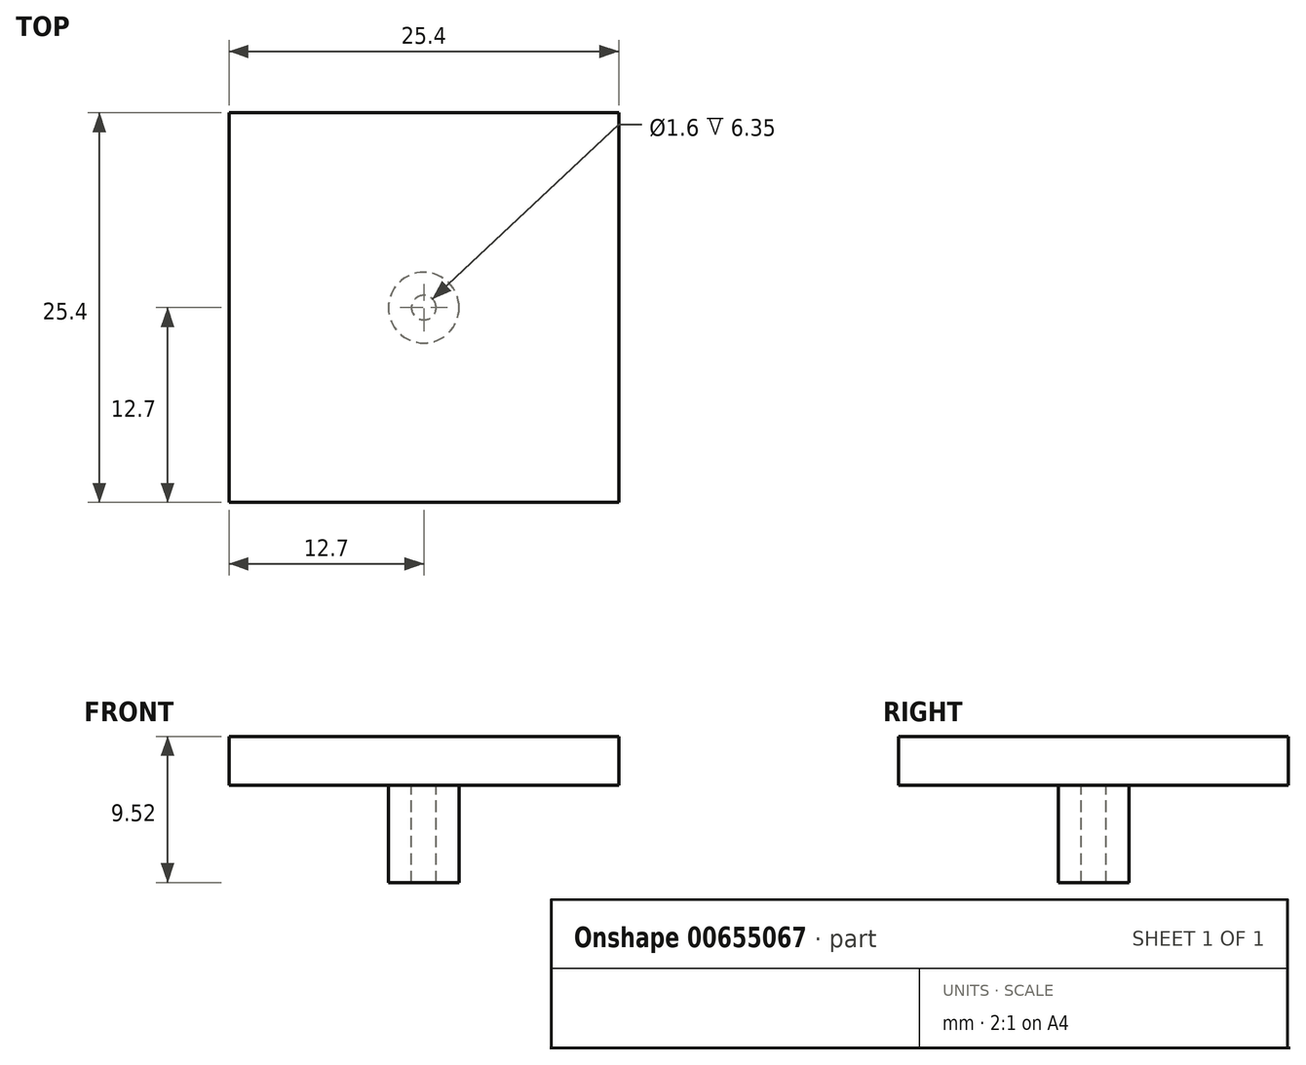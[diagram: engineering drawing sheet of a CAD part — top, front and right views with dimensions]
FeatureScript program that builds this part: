
annotation { "Feature Type Name" : "Feature", "Feature Type Description" : "" }
export const myFeature = defineFeature(function(context is Context, id is Id, definition is map)
    precondition{}
    {
        {
            var Q0;
            Q0=qCreatedBy(makeId("Top.planeOp"),FACE);
            var sketch = newSketch(context, id + "F0", { "sketchPlane" : qUnion([Q0])});
            skLineSegment(sketch, "E0.bottom", {"start": v(0, 25.4) * mm, "end": v(25.4, 25.4) * mm});
            skLineSegment(sketch, "E0.top", {"start": v(0, 0) * mm, "end": v(25.4, 0) * mm});
            skLineSegment(sketch, "E0.left", {"start": v(0, 25.4) * mm, "end": v(0, 0) * mm});
            skLineSegment(sketch, "E0.right", {"start": v(25.4, 25.4) * mm, "end": v(25.4, 0) * mm});
            skCircle(sketch, "E1", {"center": v(12.7, 12.7) * mm, "radius": 0.8 * mm});
            skCircle(sketch, "E2", {"center": v(12.7, 12.7) * mm, "radius": 2.3 * mm});
            skSolve(sketch);
        }
        {
            var Q0;
            Q0=makeQuery(id+"F0.imprint","IMPRINT",FACE,{"disambiguationData":[TD([[makeQuery(id+"F0.imprint","IMPRINT",EDGE,{"derivedFrom":sQuery(id+"F0.wireOp",EDGE,"E0.bottom")}),-1.0]])]});
            var Q1;
            Q1=makeQuery(id+"F0.imprint","IMPRINT",FACE,{"disambiguationData":[TD([[makeQuery(id+"F0.imprint","IMPRINT",EDGE,{"derivedFrom":sQuery(id+"F0.wireOp",EDGE,"E1")}),-1.0]])]});
            var Q2;
            Q2=makeQuery(id+"F0.imprint","IMPRINT",FACE,{"disambiguationData":[TD([[makeQuery(id+"F0.imprint","IMPRINT",EDGE,{"derivedFrom":sQuery(id+"F0.wireOp",EDGE,"E1")}),1.0]])]});
            extrude(context, id + "F1", {"entities" : qUnion([Q0, Q1, Q2]), "depth" : 3.17 * mm, "offsetDistance" : 25.4 * mm});
        }
        {
            var Q0;
            Q0=makeQuery(id+"F0.imprint","IMPRINT",FACE,{"disambiguationData":[TD([[makeQuery(id+"F0.imprint","IMPRINT",EDGE,{"derivedFrom":sQuery(id+"F0.wireOp",EDGE,"E1")}),-1.0]])]});
            var Q1;
            Q1=sQuery(id+"F0.wireOp",EDGE,"E1");
            var Q2;
            Q2=sQuery(id+"F0.wireOp",EDGE,"E2");
            extrude(context, id + "F2", {"entities" : qUnion([Q0]), "operationType" : NewBodyOperationType.ADD, "surfaceEntities" : qUnion([Q1, Q2]), "oppositeDirection" : true, "depth" : 6.35 * mm, "offsetDistance" : 25.4 * mm});
        }
    });
